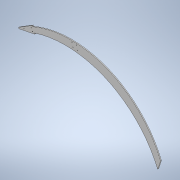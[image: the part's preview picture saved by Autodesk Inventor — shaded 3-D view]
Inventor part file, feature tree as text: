
AUTODESK INVENTOR PART (.ipt)
format: ipt  version: 2020.3 (Build 243373000, 373)  size: 200,704 bytes
history: native  units: mm
features: extrude x7, sketch x7
ambient origin geometry x8: Origin, YZ Plane, XZ Plane, XY Plane, X Axis, Y Axis, Z Axis, Center Point
bodies: Solid1 (feature_tree)
feature tree (14):
  extrude  "Extrusion1"  Depth=40.0mm
  extrude  "Extrusion2"  Depth=465.0mm
  extrude  "Extrusion4"  Depth=4.0mm TaperAngle=0.0deg
  extrude  "Extrusion6"  Depth=4.0mm TaperAngle=0.0deg
  extrude  "Extrusion7"  Depth=10.0mm TaperAngle=0.0deg
  extrude  "Extrusion8"  Depth=700.0mm
  extrude  "Extrusion9"  Depth=4.0mm
  sketch  "Sketch1"  dims[d1=30.0mm d2=40.0mm]
  sketch  "Sketch2"  dims[d4=3.490659mm d5=465.0mm]
  sketch  "Sketch4"  dims[d6=450.0mm d7=4.0mm d8=0.0mm]
  sketch  "Sketch6"  dims[d9=90.0mm d10=4.0mm d11=0.0mm]
  sketch  "Sketch7"  dims[d16=3.490659mm d17=10.0mm d18=0.0mm]
  sketch  "Sketch8"  dims[d22=700.0mm d23=1.256637mm]
  sketch  "Sketch9"  dims[d24=0.383972mm d25=1.361357mm d26=80.0mm d27=80.0mm d28=40.0mm d29=3.0mm d30=3.0mm d31=3.0mm d32=10.0mm d33=0.0mm d34=3.0mm d35=3.0mm d36=0.523599mm d38=270.0mm d39=270.0mm d40=19.024089mm d41=3.0mm d42=3.0mm d43=20.0mm d44=30.0mm d45=10.0mm d46=0.0mm d47=0.174533mm d48=270.0mm d49=0.488692mm d50=10.0mm d51=0.0mm d52=0.488692mm d53=4.0mm d54=0.0mm]
